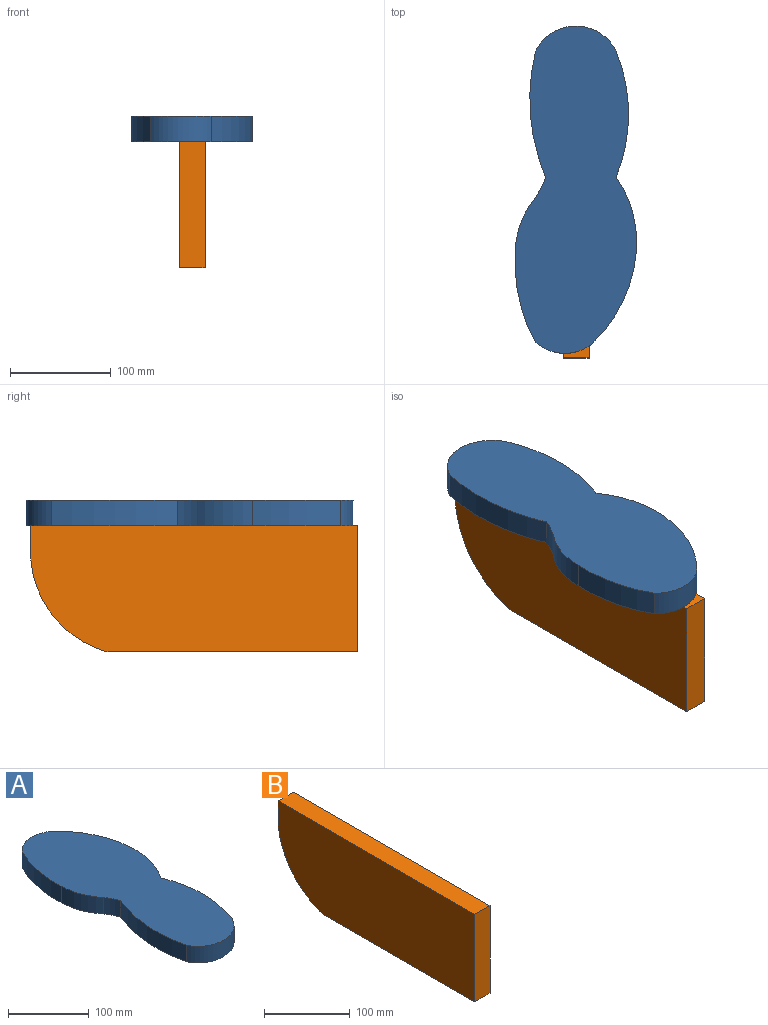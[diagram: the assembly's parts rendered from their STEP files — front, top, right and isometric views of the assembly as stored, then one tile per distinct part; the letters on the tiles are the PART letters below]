
ASSEMBLY  parts=2 mates=1
PART A: 11 faces, bbox 120.8x325x25 mm
  f0: cylinder r=42.25mm len=60mm, axis (0,0,-1), area 1668mm2, adj f1,f8,f9,f10
  f1: cylinder r=165mm len=87.5mm, axis (0,0,-1), area 2267.5mm2, adj f0,f2,f9,f10
  f2: cylinder r=85.62mm len=55mm, axis (0,0,-1), area 1493.2mm2, adj f1,f3,f9,f10
  f3: cylinder r=75mm len=25mm, axis (0,0,-1), area 561.1mm2, adj f2,f4,f9,f10
  f4: cylinder r=200mm len=125mm, axis (0,0,-1), area 3188.7mm2, adj f3,f5,f9,f10
  f5: cylinder r=44.5mm len=80mm, axis (0,0,-1), area 2485.8mm2, adj f4,f6,f9,f10
  f6: cylinder r=165mm len=125mm, axis (0,0,-1), area 3205mm2, adj f5,f7,f9,f10
  f7: cylinder r=112mm len=75mm, axis (0,0,-1), area 1981.6mm2, adj f6,f8,f9,f10
  f8: cylinder r=143.2mm len=87.5mm, axis (0,0,-1), area 2462.9mm2, adj f0,f7,f9,f10
  f9: plane 325x120.78mm, normal (0,0,1), area 29744.8mm2, adj f0,f1,f2,f3,f4,f5,f6,f7
  f10: plane 325x120.78mm, normal (0,0,-1), area 29744.8mm2, adj f0,f1,f2,f3,f4,f5,f6,f7
PART B: 7 faces, bbox 25x325x125 mm
  f0: plane 325x25mm, normal (0,0,1), area 8125mm2, adj f1,f4,f5,f6
  f1: plane 125x25mm, normal (0,-1,0), area 3125mm2, adj f0,f2,f5,f6
  f2: plane 250x25mm, normal (0,0,-1), area 6250mm2, adj f1,f3,f5,f6
  f3: cylinder r=104.17mm len=100mm, axis (-1,0,0), area 3351.6mm2, adj f2,f4,f5,f6
  f4: plane 25x25mm, normal (0,1,0), area 625mm2, adj f0,f3,f5,f6
  f5: plane 325x125mm, normal (1,0,0), area 38649.1mm2, adj f0,f1,f2,f3,f4
  f6: plane 325x125mm, normal (-1,0,0), area 38649.1mm2, adj f0,f1,f2,f3,f4
PLACE A rot(axis=(1,0,0),180deg) t=(-0.6,16.77,0)mm
PLACE B t=(0,-12.5,-25)mm
MATE fastened B.f0 <-> A.f9  axis (0,0,1) through (0,0,-25)mm
